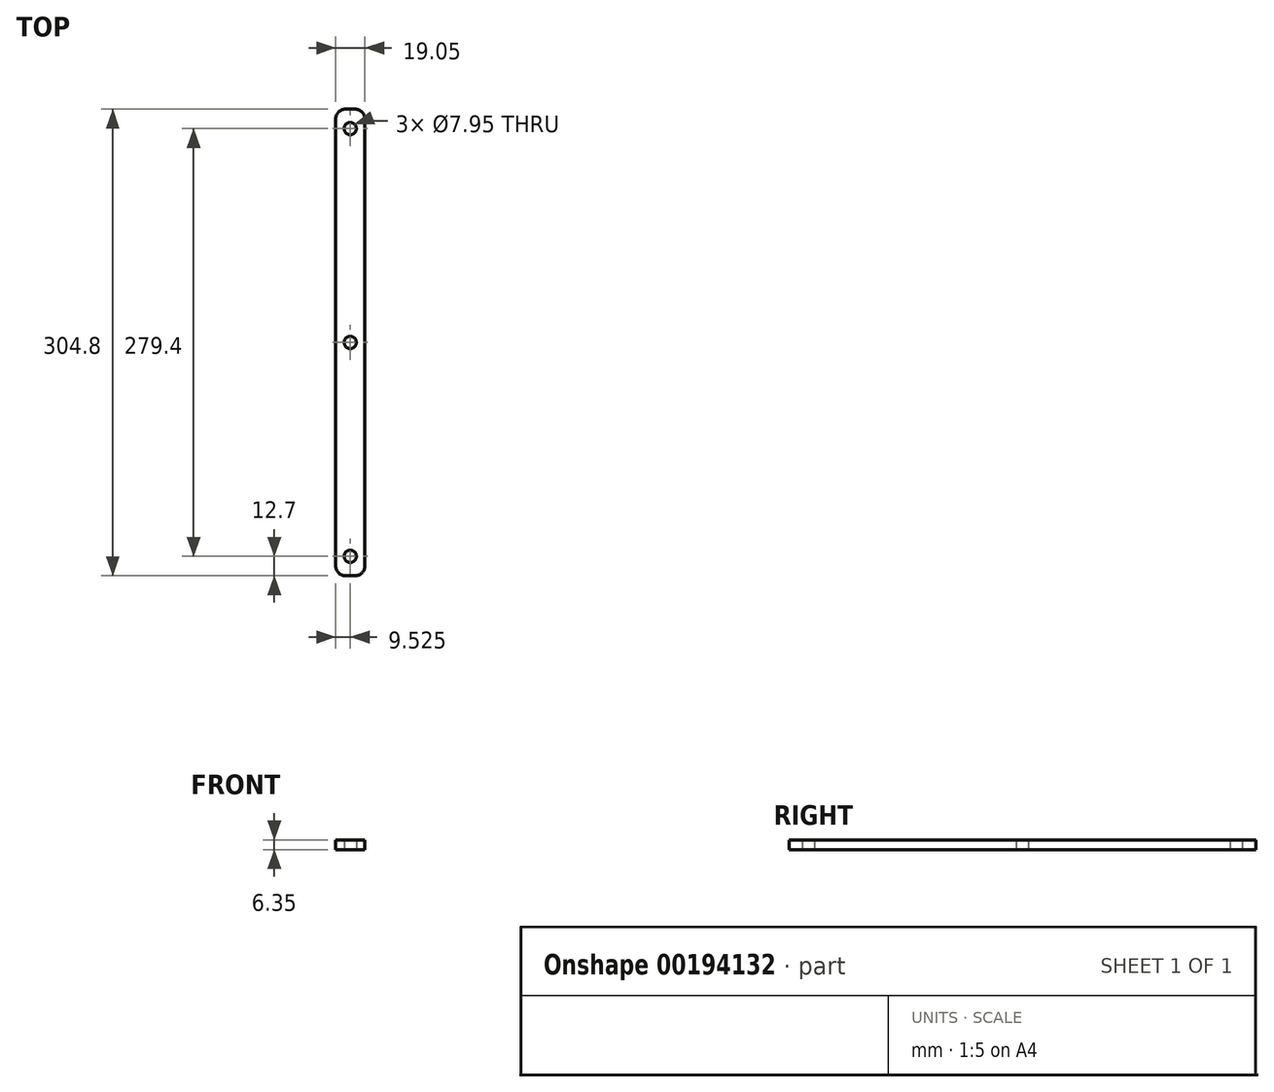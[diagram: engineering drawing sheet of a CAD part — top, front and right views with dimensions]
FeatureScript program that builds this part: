
annotation { "Feature Type Name" : "Feature", "Feature Type Description" : "" }
export const myFeature = defineFeature(function(context is Context, id is Id, definition is map)
    precondition{}
    {
        {
            var Q0;
            Q0=qCreatedBy(makeId("Top.planeOp"),FACE);
            var sketch = newSketch(context, id + "F0", { "sketchPlane" : qUnion([Q0])});
            skLineSegment(sketch, "E0.bottom", {"start": v(6.35, 0) * mm, "end": v(12.7, 0) * mm});
            skLineSegment(sketch, "E0.top", {"start": v(6.35, 304.8) * mm, "end": v(12.7, 304.8) * mm});
            skLineSegment(sketch, "E0.left", {"start": v(0, 6.35) * mm, "end": v(0, 298.45) * mm});
            skLineSegment(sketch, "E0.right", {"start": v(19.05, 6.35) * mm, "end": v(19.05, 298.45) * mm});
            skCircle(sketch, "E1", {"center": v(9.53, 12.7) * mm, "radius": 3.98 * mm});
            skPoint(sketch, "E1.centerSnap0", {"position": v(9.53, 0) * mm});
            skLineSegment(sketch, "E2", {"start": v(0, 152.4) * mm, "end": v(19.05, 152.4) * mm, "construction": true});
            skCircle(sketch, "E3.MirrorC", {"center": v(9.53, 292.1) * mm, "radius": 3.98 * mm});
            skPoint(sketch, "E4.visualSharp", {"position": v(0, 304.8) * mm});
            skArc(sketch, "E4.filletArc", {"start": v(6.35, 304.8) * mm, "mid": v(1.86, 302.94) * mm, "end": v(0, 298.45) * mm});
            skPoint(sketch, "E5.visualSharp", {"position": v(19.05, 304.8) * mm});
            skArc(sketch, "E5.filletArc", {"start": v(19.05, 298.45) * mm, "mid": v(17.2, 302.94) * mm, "end": v(12.7, 304.8) * mm});
            skPoint(sketch, "E6.visualSharp", {"position": v(0, 0) * mm});
            skArc(sketch, "E6.filletArc", {"start": v(0, 6.35) * mm, "mid": v(1.86, 1.86) * mm, "end": v(6.35, 0) * mm});
            skPoint(sketch, "E7.visualSharp", {"position": v(19.05, 0) * mm});
            skArc(sketch, "E7.filletArc", {"start": v(12.7, 0) * mm, "mid": v(17.2, 1.86) * mm, "end": v(19.05, 6.35) * mm});
            skCircle(sketch, "E8", {"center": v(9.52, 152.4) * mm, "radius": 3.98 * mm});
            skSolve(sketch);
        }
        {
            var Q0;
            Q0=makeQuery(id+"F0.imprint","IMPRINT",FACE,{"disambiguationData":[TD([[makeQuery(id+"F0.imprint","IMPRINT",EDGE,{"derivedFrom":sQuery(id+"F0.wireOp",EDGE,"E0.bottom")}),1.0]])]});
            extrude(context, id + "F1", {"entities" : qUnion([Q0]), "depth" : 6.35 * mm});
        }
    });
